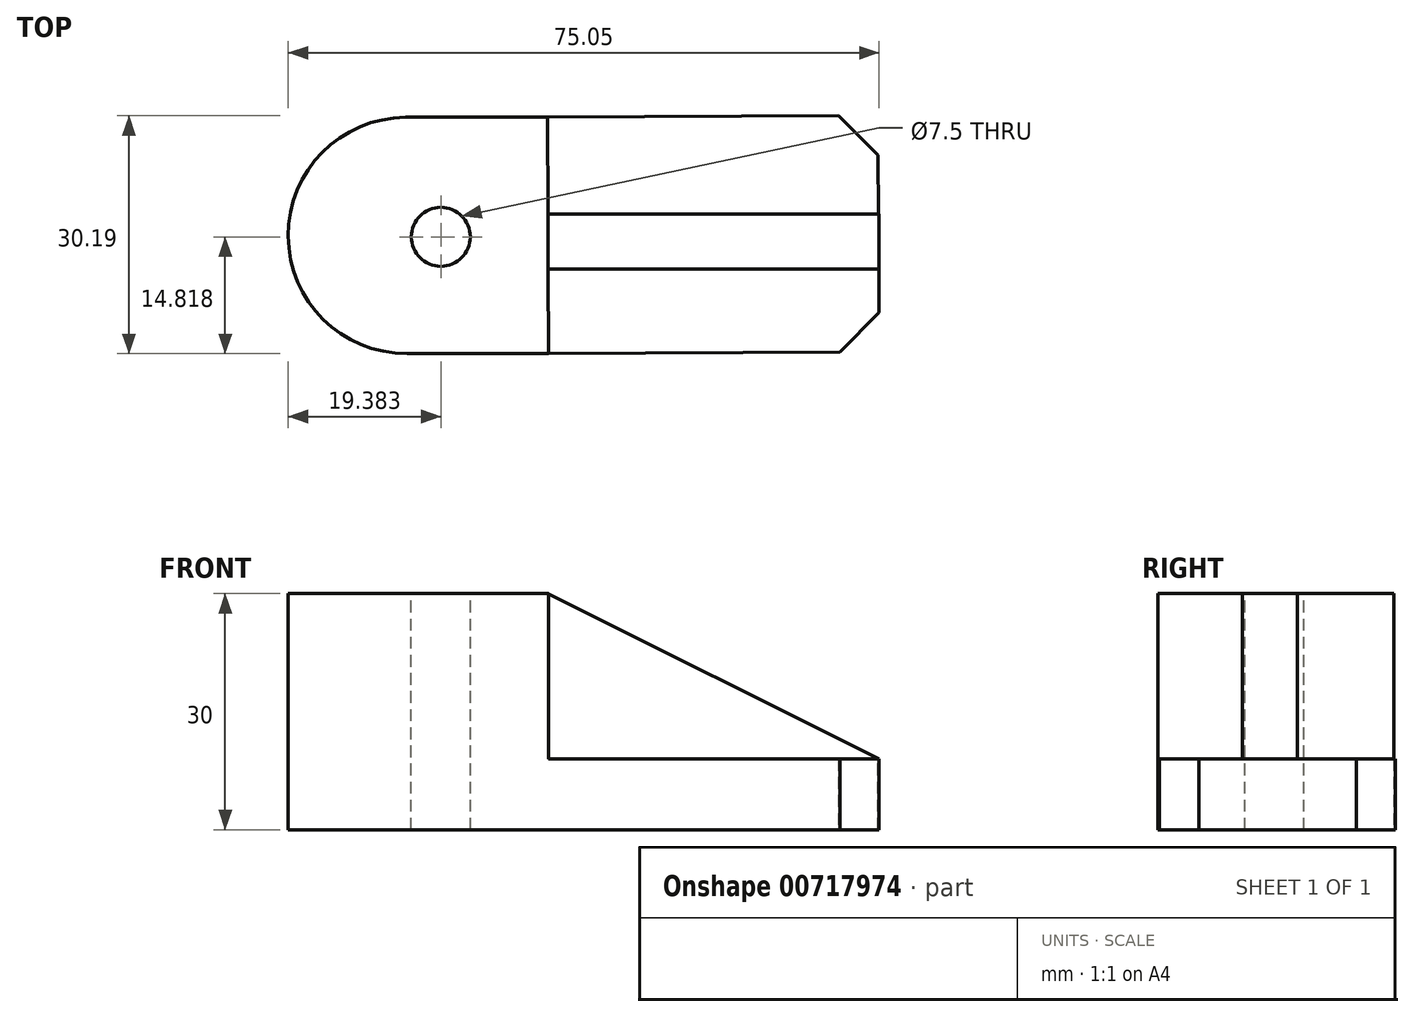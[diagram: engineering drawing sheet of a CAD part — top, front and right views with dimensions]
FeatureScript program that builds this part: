
annotation { "Feature Type Name" : "Feature", "Feature Type Description" : "" }
export const myFeature = defineFeature(function(context is Context, id is Id, definition is map)
    precondition{}
    {
        {
            var Q0;
            Q0=qCreatedBy(makeId("Top.planeOp"),FACE);
            var sketch = newSketch(context, id + "F0", { "sketchPlane" : qUnion([Q0])});
            skLineSegment(sketch, "E0", {"start": v(8.58, 19.29) * mm, "end": v(-9.42, 19.29) * mm});
            skLineSegment(sketch, "E1", {"start": v(8.74, -10.71) * mm, "end": v(-9.26, -10.71) * mm});
            skArc(sketch, "E2", {"start": v(-9.42, 19.29) * mm, "mid": v(-24.34, 4.2) * mm, "end": v(-9.26, -10.71) * mm});
            skLineSegment(sketch, "E3", {"start": v(8.58, 19.29) * mm, "end": v(8.74, -10.71) * mm});
            skSolve(sketch);
        }
        {
            var Q0;
            Q0 = qSketchRegion(id + "F0", true);
            extrude(context, id + "F1", {"entities" : qUnion([Q0]), "depth" : 30 * mm, "offsetDistance" : 25 * mm});
        }
        {
            var Q0;
            Q0=makeQuery(id+"F1.opExtrude","CAP_FACE",FACE,{"disambiguationData":[OSD([sQuery(id+"F0.wireOp",EDGE,"E0"),sQuery(id+"F0.wireOp",EDGE,"E1"),sQuery(id+"F0.wireOp",EDGE,"E2"),sQuery(id+"F0.wireOp",EDGE,"E3")])],"isStart":false});
            var sketch = newSketch(context, id + "F2", { "sketchPlane" : qUnion([Q0])});
            skCircle(sketch, "E4", {"center": v(-4.96, 4.1) * mm, "radius": 3.75 * mm});
            skSolve(sketch);
        }
        {
            var Q0;
            Q0 = qSketchRegion(id + "F2", true);
            extrude(context, id + "F3", {"entities" : qUnion([Q0]), "operationType" : NewBodyOperationType.REMOVE, "oppositeDirection" : true, "depth" : 30 * mm, "offsetDistance" : 25 * mm});
        }
        {
            var Q0;
            Q0=makeQuery(id+"F1.opExtrude","SWEPT_FACE",FACE,{"disambiguationData":[OSD([sQuery(id+"F0.wireOp",EDGE,"E3")])]});
            var sketch = newSketch(context, id + "F4", { "sketchPlane" : qUnion([Q0])});
            skLineSegment(sketch, "E5.bottom", {"start": v(-10.76, 0) * mm, "end": v(19.24, 0) * mm});
            skLineSegment(sketch, "E5.top", {"start": v(-10.76, 9) * mm, "end": v(19.24, 9) * mm});
            skLineSegment(sketch, "E5.left", {"start": v(-10.76, 0) * mm, "end": v(-10.76, 9) * mm});
            skLineSegment(sketch, "E5.right", {"start": v(19.24, 0) * mm, "end": v(19.24, 9) * mm});
            skSolve(sketch);
        }
        {
            var Q0;
            Q0=makeQuery(id+"F4.imprint","IMPRINT",FACE,{"disambiguationData":[TD([[makeQuery(id+"F4.imprint","IMPRINT",EDGE,{"derivedFrom":sQuery(id+"F4.wireOp",EDGE,"E5.bottom")}),-1.0]])]});
            extrude(context, id + "F5", {"entities" : qUnion([Q0]), "operationType" : NewBodyOperationType.ADD, "depth" : 42 * mm, "offsetDistance" : 25 * mm});
        }
        {
            var Q0;
            Q0=makeQuery(id+"F5.opExtrude","CAP_EDGE",EDGE,{"disambiguationData":[OSD([sQuery(id+"F4.wireOp",EDGE,"E5.left")])],"isStart":false});
            var Q1;
            Q1=makeQuery(id+"F5.opExtrude","CAP_EDGE",EDGE,{"disambiguationData":[OSD([sQuery(id+"F4.wireOp",EDGE,"E5.right")])],"isStart":false});
            chamfer(context, id + "F6", {"entities" : qUnion([Q0, Q1]), "width" : 5 * mm, "tangentPropagation" : true});
        }
        {
            var Q0;
            Q0=makeQuery(id+"F5.opExtrude","SWEPT_FACE",FACE,{"disambiguationData":[OSD([sQuery(id+"F4.wireOp",EDGE,"E5.top")])]});
            var sketch = newSketch(context, id + "F7", { "sketchPlane" : qUnion([Q0])});
            skLineSegment(sketch, "E6.bottom", {"start": v(50.68, 0) * mm, "end": v(50.64, 0) * mm});
            skLineSegment(sketch, "E6.top", {"start": v(50.68, 6.47) * mm, "end": v(50.64, 6.47) * mm});
            skLineSegment(sketch, "E6.left", {"start": v(50.68, 0) * mm, "end": v(50.68, 6.47) * mm});
            skLineSegment(sketch, "E6.right", {"start": v(50.64, 0) * mm, "end": v(50.64, 6.47) * mm});
            skLineSegment(sketch, "E7.bottom", {"start": v(50.68, 0) * mm, "end": v(8.64, 0) * mm});
            skLineSegment(sketch, "E7.top", {"start": v(50.68, 7) * mm, "end": v(8.64, 7) * mm});
            skLineSegment(sketch, "E7.left", {"start": v(50.68, 0) * mm, "end": v(50.68, 7) * mm});
            skLineSegment(sketch, "E7.right", {"start": v(8.64, 0) * mm, "end": v(8.64, 7) * mm});
            skSolve(sketch);
        }
        {
            var Q0;
            Q0 = qSketchRegion(id + "F7", true);
            extrude(context, id + "F8", {"entities" : qUnion([Q0]), "operationType" : NewBodyOperationType.ADD, "depth" : 21 * mm, "offsetDistance" : 25 * mm});
        }
        {
            var Q0;
            Q0=makeQuery(id+"F8.opExtrude","SWEPT_FACE",FACE,{"disambiguationData":[OSD([sQuery(id+"F7.wireOp",EDGE,"E7.bottom")])]});
            var sketch = newSketch(context, id + "F9", { "sketchPlane" : qUnion([Q0])});
            skLineSegment(sketch, "E8", {"start": v(8.68, 30) * mm, "end": v(50.68, 9) * mm});
            skLineSegment(sketch, "E9", {"start": v(50.68, 9) * mm, "end": v(50.68, 30) * mm});
            skLineSegment(sketch, "E10", {"start": v(50.68, 30) * mm, "end": v(8.68, 30) * mm});
            skSolve(sketch);
        }
        {
            var Q0;
            Q0 = qSketchRegion(id + "F9", true);
            extrude(context, id + "F10", {"entities" : qUnion([Q0]), "operationType" : NewBodyOperationType.REMOVE, "oppositeDirection" : true, "depth" : 25 * mm, "offsetDistance" : 25 * mm});
        }
    });
